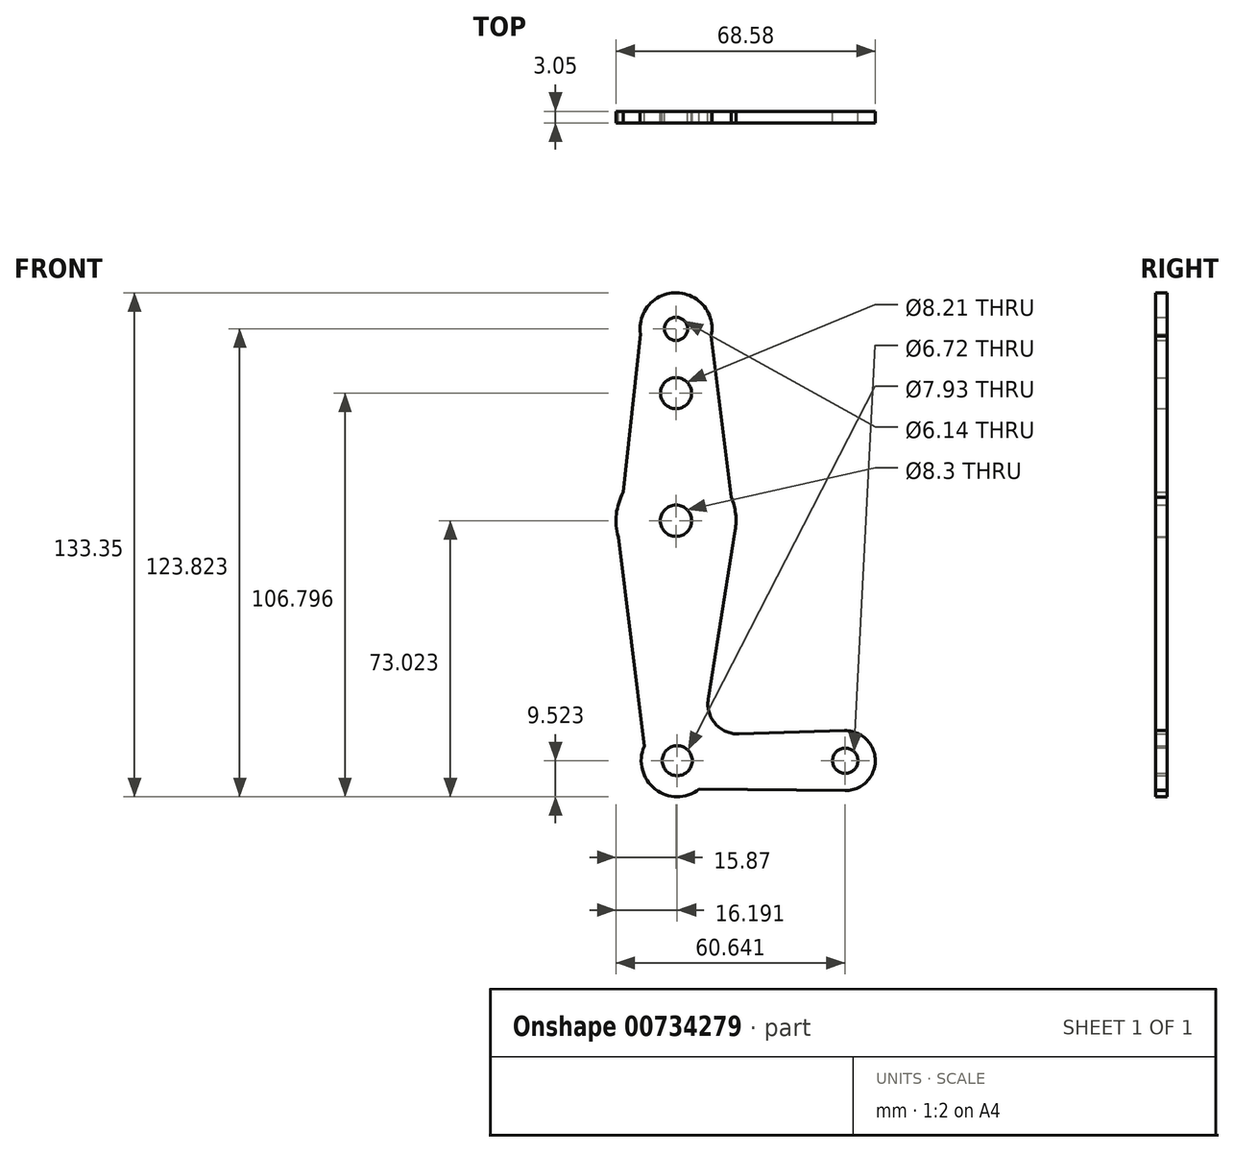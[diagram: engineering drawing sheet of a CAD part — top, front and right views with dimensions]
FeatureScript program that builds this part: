
annotation { "Feature Type Name" : "Feature", "Feature Type Description" : "" }
export const myFeature = defineFeature(function(context is Context, id is Id, definition is map)
    precondition{}
    {
        {
            var Q0;
            Q0=qCreatedBy(makeId("Front.planeOp"),FACE);
            var sketch = newSketch(context, id + "F0", { "sketchPlane" : qUnion([Q0])});
            skLineSegment(sketch, "E0", {"start": v(-31.43, 65.25) * mm, "end": v(-31.43, -67.1) * mm, "construction": true});
            skLineSegment(sketch, "E1", {"start": v(-31.1, -49.05) * mm, "end": v(13.34, -49.05) * mm, "construction": true});
            skCircle(sketch, "E2", {"center": v(-31.43, 65.25) * mm, "radius": 9.53 * mm});
            skCircle(sketch, "E3", {"center": v(-31.43, 14.45) * mm, "radius": 15.88 * mm});
            skCircle(sketch, "E4", {"center": v(-31.1, -49.05) * mm, "radius": 9.53 * mm});
            skCircle(sketch, "E5", {"center": v(13.34, -49.05) * mm, "radius": 7.94 * mm});
            skLineSegment(sketch, "E6", {"start": v(-46.69, 10.08) * mm, "end": v(-39.85, -45.27) * mm});
            skLineSegment(sketch, "E7", {"start": v(-15.74, 12.02) * mm, "end": v(-22.9, -32.77) * mm});
            skLineSegment(sketch, "E8", {"start": v(-14.8, -41.97) * mm, "end": v(13.1, -41.11) * mm});
            skLineSegment(sketch, "E9", {"start": v(-25.3, -56.6) * mm, "end": v(13.26, -56.98) * mm});
            skLineSegment(sketch, "E10", {"start": v(-22.1, 63.36) * mm, "end": v(-15.74, 12.02) * mm});
            skPoint(sketch, "E11.visualSharp", {"position": v(-24.42, -42.27) * mm});
            skArc(sketch, "E11.filletArc", {"start": v(-22.9, -32.77) * mm, "mid": v(-21.02, -39.28) * mm, "end": v(-14.8, -41.97) * mm});
            skCircle(sketch, "E12", {"center": v(-31.43, 65.25) * mm, "radius": 3.07 * mm});
            skCircle(sketch, "E13", {"center": v(-31.43, 14.45) * mm, "radius": 4.15 * mm});
            skCircle(sketch, "E14", {"center": v(-31.1, -49.05) * mm, "radius": 3.97 * mm});
            skCircle(sketch, "E15", {"center": v(13.34, -49.05) * mm, "radius": 3.36 * mm});
            skCircle(sketch, "E16", {"center": v(-31.43, 48.23) * mm, "radius": 4.1 * mm});
            skLineSegment(sketch, "E17", {"start": v(-46.69, 10.08) * mm, "end": v(-40.85, 63.86) * mm});
            skSolve(sketch);
        }
        {
            var Q0;
            Q0 = qSketchRegion(id + "F0", true);
            extrude(context, id + "F1", {"entities" : qUnion([Q0]), "depth" : 3.05 * mm, "offsetDistance" : 25.4 * mm});
        }
    });
